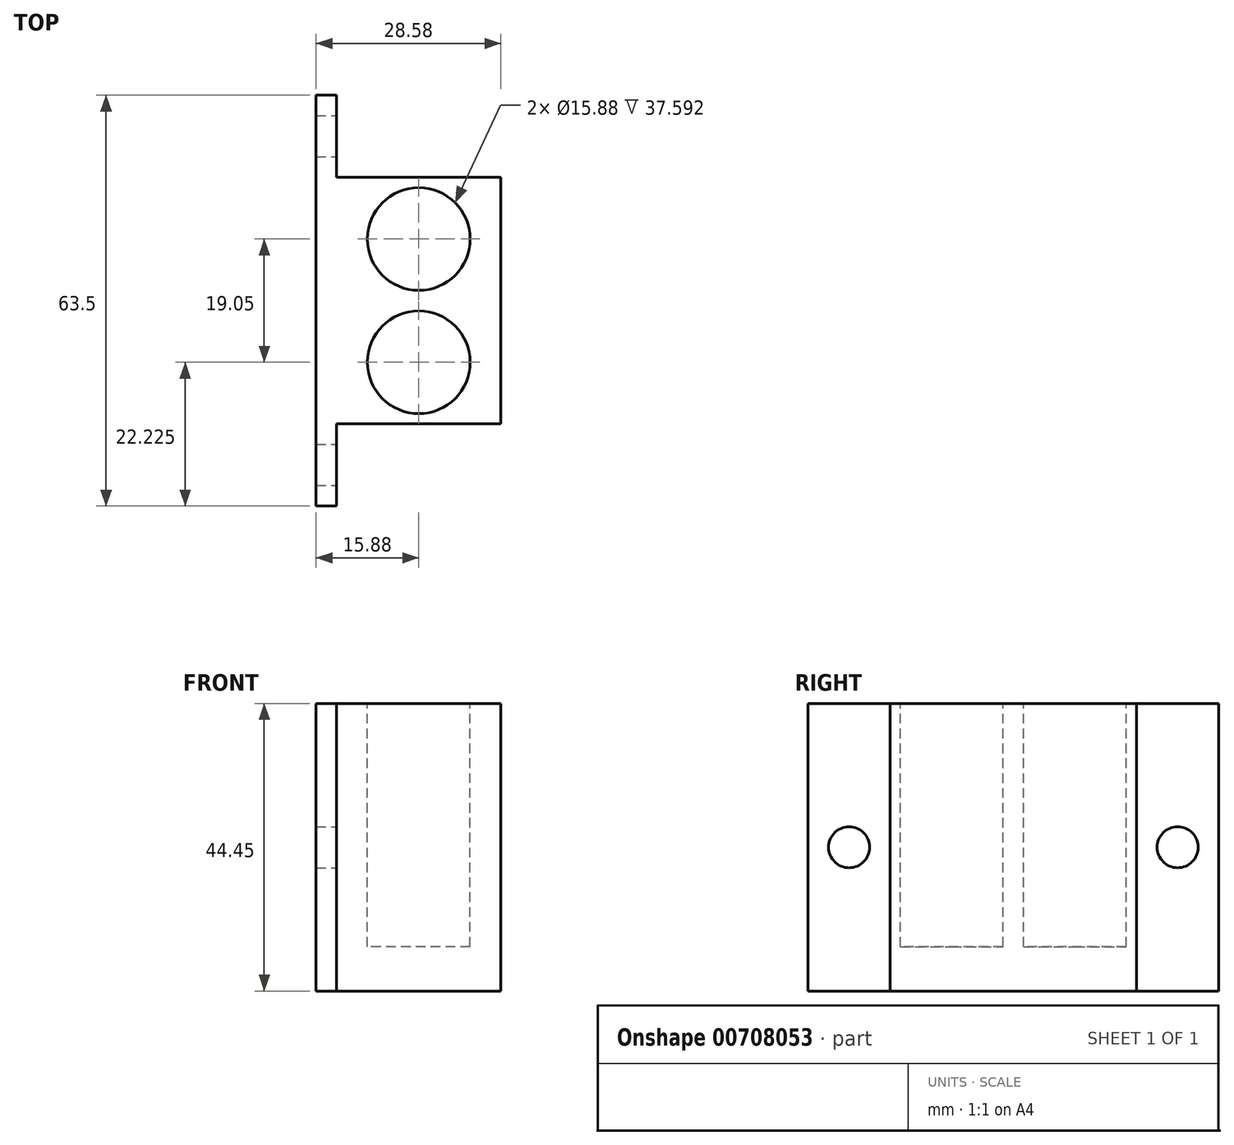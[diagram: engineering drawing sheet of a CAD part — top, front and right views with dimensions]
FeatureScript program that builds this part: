
annotation { "Feature Type Name" : "Feature", "Feature Type Description" : "" }
export const myFeature = defineFeature(function(context is Context, id is Id, definition is map)
    precondition{}
    {
        {
            var Q0;
            Q0=qCreatedBy(makeId("Right.planeOp"),FACE);
            var sketch = newSketch(context, id + "F0", { "sketchPlane" : qUnion([Q0])});
            skLineSegment(sketch, "E0.bottom", {"start": v(0, 0) * mm, "end": v(38.1, 0) * mm});
            skLineSegment(sketch, "E0.top", {"start": v(0, 19.05) * mm, "end": v(38.1, 19.05) * mm});
            skLineSegment(sketch, "E0.left", {"start": v(0, 0) * mm, "end": v(0, 19.05) * mm});
            skLineSegment(sketch, "E0.right", {"start": v(38.1, 0) * mm, "end": v(38.1, 19.05) * mm});
            skSolve(sketch);
        }
        {
            var Q0;
            Q0=makeQuery(id+"F0.imprint","IMPRINT",FACE,{"disambiguationData":[TD([[makeQuery(id+"F0.imprint","IMPRINT",EDGE,{"derivedFrom":sQuery(id+"F0.wireOp",EDGE,"E0.bottom")}),1.0]])]});
            extrude(context, id + "F1", {"entities" : qUnion([Q0]), "depth" : 25.4 * mm, "offsetDistance" : 25.4 * mm});
        }
        {
            var Q0;
            Q0=makeQuery(id+"F1.opExtrude","SWEPT_FACE",FACE,{"disambiguationData":[OSD([sQuery(id+"F0.wireOp",EDGE,"E0.top")])]});
            var sketch = newSketch(context, id + "F2", { "sketchPlane" : qUnion([Q0])});
            skCircle(sketch, "E1", {"center": v(12.7, 28.58) * mm, "radius": 7.94 * mm});
            skCircle(sketch, "E2", {"center": v(12.7, 9.53) * mm, "radius": 7.94 * mm});
            skPoint(sketch, "E3.start.orphan", {"position": v(12.7, 38.1) * mm});
            skPoint(sketch, "E4.orphan", {"position": v(12.7, 19.05) * mm});
            skPoint(sketch, "E5.start.orphan", {"position": v(12.7, 0) * mm});
            skSolve(sketch);
        }
        {
            var Q0;
            Q0=makeQuery(id+"F1.opExtrude","SWEPT_FACE",FACE,{"disambiguationData":[OSD([sQuery(id+"F0.wireOp",EDGE,"E0.bottom")])]});
            extrude(context, id + "F3", {"entities" : qUnion([Q0]), "operationType" : NewBodyOperationType.ADD, "depth" : 25.4 * mm, "offsetDistance" : 25.4 * mm});
        }
        {
            var Q0;
            Q0=makeQuery(id+"F2.imprint","IMPRINT",FACE,{"disambiguationData":[TD([[makeQuery(id+"F2.imprint","IMPRINT",EDGE,{"derivedFrom":sQuery(id+"F2.wireOp",EDGE,"E1")}),1.0]])]});
            var Q1;
            Q1=makeQuery(id+"F2.imprint","IMPRINT",FACE,{"disambiguationData":[TD([[makeQuery(id+"F2.imprint","IMPRINT",EDGE,{"derivedFrom":sQuery(id+"F2.wireOp",EDGE,"E2")}),1.0]])]});
            extrude(context, id + "F4", {"entities" : qUnion([Q0, Q1]), "operationType" : NewBodyOperationType.REMOVE, "oppositeDirection" : true, "depth" : 37.6 * mm, "offsetDistance" : 25.4 * mm});
        }
        {
            var Q0;
            {var subQ0=sQuery(id+"F0.wireOp",EDGE,"E0.bottom");Q0=makeQuery(id+"F3.boolean.opBoolean","MERGE",FACE,{"derivedFrom":[makeQuery(id+"F1.opExtrude","CAP_FACE",FACE,{"disambiguationData":[OSD([subQ0,sQuery(id+"F0.wireOp",EDGE,"E0.top"),sQuery(id+"F0.wireOp",EDGE,"E0.left"),sQuery(id+"F0.wireOp",EDGE,"E0.right")])],"isStart":true}),makeQuery(id+"F3.opExtrude","SWEPT_FACE",FACE,{"disambiguationData":[OSD([subQ0]),TDD([makeQuery(id+"F1.opExtrude","CAP_EDGE",EDGE,{"disambiguationData":[OSD([subQ0])],"isStart":true})])]})]});}
            var sketch = newSketch(context, id + "F5", { "sketchPlane" : qUnion([Q0])});
            skLineSegment(sketch, "E6.top", {"start": v(-50.8, 19.05) * mm, "end": v(12.7, 19.05) * mm});
            skLineSegment(sketch, "E6.left", {"start": v(-50.8, -25.4) * mm, "end": v(-50.8, 19.05) * mm});
            skLineSegment(sketch, "E6.right", {"start": v(12.7, -25.4) * mm, "end": v(12.7, 19.05) * mm});
            skLineSegment(sketch, "E7.trimOffspring", {"start": v(-38.1, -25.4) * mm, "end": v(12.7, -25.4) * mm});
            skLineSegment(sketch, "E8", {"start": v(-50.8, -25.4) * mm, "end": v(-38.1, -25.4) * mm});
            skSolve(sketch);
        }
        {
            var Q0;
            {var subQ4=sQuery(id+"F5.wireOp",EDGE,"E6.left");Q0=makeQuery(id+"F5.imprint","IMPRINT",FACE,{"disambiguationData":[TD([[makeQuery(id+"F5.imprint","IMPRINT",EDGE,{"derivedFrom":subQ4}),-1.0]])]});}
            var Q1;
            {var subQ1=sQuery(id+"F0.wireOp",EDGE,"E0.left");var subQ2=sQuery(id+"F0.wireOp",EDGE,"E0.bottom");var subQ3=makeQuery(id+"F3.boolean.opBoolean","MERGE",EDGE,{"derivedFrom":[makeQuery(id+"F1.opExtrude","CAP_EDGE",EDGE,{"disambiguationData":[OSD([subQ1])],"isStart":true}),makeQuery(id+"F3.opExtrude","SWEPT_EDGE",EDGE,{"disambiguationData":[OSD([subQ2,subQ1]),TDD([makeQuery(id+"F1.opExtrude","CAP_VERTEX",VERTEX,{"disambiguationData":[OSD([subQ2,subQ1])],"isStart":true})])]})]});Q1=makeQuery(id+"F5.imprint","IMPRINT",FACE,{"disambiguationData":[TD([[makeQuery(id+"F5.imprint","IMPRINT",EDGE,{"derivedFrom":subQ3}),1.0]])]});}
            var Q2;
            {var subQ4=sQuery(id+"F5.wireOp",EDGE,"E6.right");Q2=makeQuery(id+"F5.imprint","IMPRINT",FACE,{"disambiguationData":[TD([[makeQuery(id+"F5.imprint","IMPRINT",EDGE,{"derivedFrom":subQ4}),1.0]])]});}
            extrude(context, id + "F6", {"entities" : qUnion([Q0, Q1, Q2]), "operationType" : NewBodyOperationType.ADD, "depth" : 3.17 * mm, "offsetDistance" : 25.4 * mm});
        }
        {
            var Q0;
            {var subQ0=sQuery(id+"F0.wireOp",EDGE,"E0.right");var subQ2=sQuery(id+"F5.wireOp",EDGE,"E6.left");var subQ3=sQuery(id+"F5.wireOp",EDGE,"E6.top");var subQ4=sQuery(id+"F5.wireOp",EDGE,"E8");var subQ5=sQuery(id+"F5.wireOp",EDGE,"E7.trimOffspring");Q0=makeQuery(id+"F6.boolean.opBoolean","SPLIT",FACE,{"disambiguationData":[TD([makeQuery(id+"F1.opExtrude","SWEPT_FACE",FACE,{"disambiguationData":[OSD([subQ0])]})])],"derivedFrom":makeQuery(id+"F6.opExtrude","CAP_FACE",FACE,{"disambiguationData":[OSD([subQ3,subQ2,sQuery(id+"F5.wireOp",EDGE,"E6.right"),subQ5,subQ4])],"isStart":true})});}
            var sketch = newSketch(context, id + "F7", { "sketchPlane" : qUnion([Q0])});
            skLineSegment(sketch, "E9", {"start": v(38.1, 19.05) * mm, "end": v(50.8, -25.4) * mm, "construction": true});
            skLineSegment(sketch, "E10", {"start": v(38.1, -25.4) * mm, "end": v(50.8, 19.05) * mm, "construction": true});
            skCircle(sketch, "E11", {"center": v(44.45, -3.18) * mm, "radius": 3.18 * mm});
            skSolve(sketch);
        }
        {
            var Q0;
            {var subQ0=sQuery(id+"F0.wireOp",EDGE,"E0.left");var subQ2=sQuery(id+"F5.wireOp",EDGE,"E6.top");var subQ3=sQuery(id+"F5.wireOp",EDGE,"E6.right");var subQ4=sQuery(id+"F5.wireOp",EDGE,"E8");var subQ5=sQuery(id+"F5.wireOp",EDGE,"E7.trimOffspring");Q0=makeQuery(id+"F6.boolean.opBoolean","SPLIT",FACE,{"disambiguationData":[TD([makeQuery(id+"F1.opExtrude","SWEPT_FACE",FACE,{"disambiguationData":[OSD([subQ0])]})])],"derivedFrom":makeQuery(id+"F6.opExtrude","CAP_FACE",FACE,{"disambiguationData":[OSD([subQ2,sQuery(id+"F5.wireOp",EDGE,"E6.left"),subQ3,subQ5,subQ4])],"isStart":true})});}
            var sketch = newSketch(context, id + "F8", { "sketchPlane" : qUnion([Q0])});
            skLineSegment(sketch, "E12", {"start": v(-12.7, -25.4) * mm, "end": v(0, 19.05) * mm, "construction": true});
            skLineSegment(sketch, "E13", {"start": v(-12.7, 19.05) * mm, "end": v(0, -25.4) * mm, "construction": true});
            skCircle(sketch, "E14", {"center": v(-6.35, -3.18) * mm, "radius": 3.18 * mm});
            skSolve(sketch);
        }
        {
            var Q0;
            Q0=makeQuery(id+"F8.imprint","IMPRINT",FACE,{"disambiguationData":[TD([[makeQuery(id+"F8.imprint","IMPRINT",EDGE,{"derivedFrom":sQuery(id+"F8.wireOp",EDGE,"E14")}),1.0]])]});
            var Q1;
            Q1=makeQuery(id+"F7.imprint","IMPRINT",FACE,{"disambiguationData":[TD([[makeQuery(id+"F7.imprint","IMPRINT",EDGE,{"derivedFrom":sQuery(id+"F7.wireOp",EDGE,"E11")}),1.0]])]});
            extrude(context, id + "F9", {"entities" : qUnion([Q0, Q1]), "operationType" : NewBodyOperationType.REMOVE, "oppositeDirection" : true, "depth" : 25.4 * mm, "offsetDistance" : 25.4 * mm});
        }
    });
